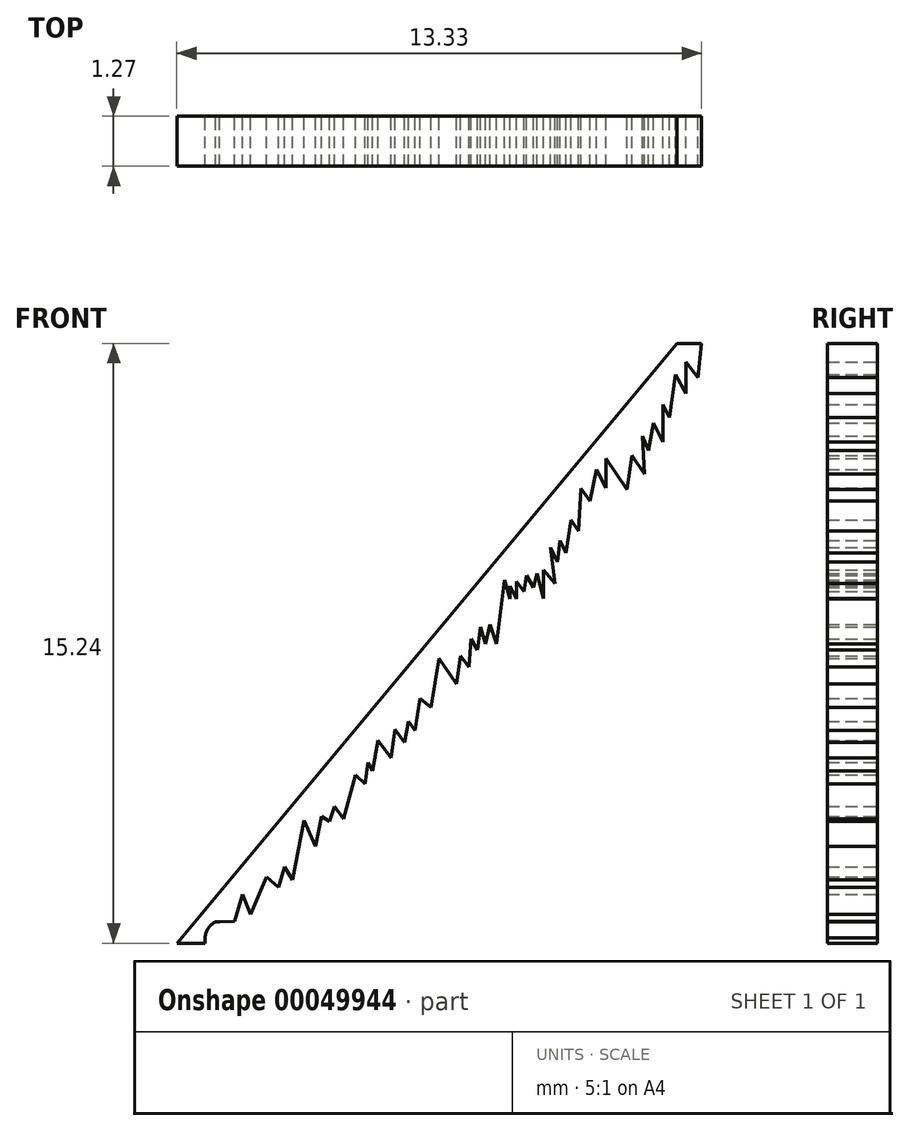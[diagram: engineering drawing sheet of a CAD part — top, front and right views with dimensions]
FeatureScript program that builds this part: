
annotation { "Feature Type Name" : "Feature", "Feature Type Description" : "" }
export const myFeature = defineFeature(function(context is Context, id is Id, definition is map)
    precondition{}
    {
        {
            var Q0;
            Q0=qCreatedBy(makeId("Front.planeOp"),FACE);
            var sketch = newSketch(context, id + "F0", { "sketchPlane" : qUnion([Q0])});
            skLineSegment(sketch, "E0", {"start": v(6.44, 7.64) * mm, "end": v(-6.26, -7.6) * mm});
            skLineSegment(sketch, "E1", {"start": v(-6.26, -7.6) * mm, "end": v(-5.63, -7.6) * mm});
            skLineSegment(sketch, "E2", {"start": v(6.44, 7.64) * mm, "end": v(7.07, 7.64) * mm});
            skLineSegment(sketch, "E3", {"start": v(-4.6, -6.36) * mm, "end": v(-4.17, -6.36) * mm});
            skLineSegment(sketch, "E4", {"start": v(-4.38, -6.36) * mm, "end": v(-4.38, -6.87) * mm});
            skLineSegment(sketch, "E5", {"start": v(-4.38, -6.87) * mm, "end": v(-4.17, -6.36) * mm});
            skLineSegment(sketch, "E6", {"start": v(-4.6, -6.36) * mm, "end": v(-4.38, -6.87) * mm});
            skLineSegment(sketch, "E7", {"start": v(-4.38, -6.87) * mm, "end": v(-3.73, -5.33) * mm});
            skLineSegment(sketch, "E8", {"start": v(-3.73, -5.33) * mm, "end": v(-3.32, -6) * mm});
            skLineSegment(sketch, "E9", {"start": v(-3.32, -6) * mm, "end": v(-3.02, -4.48) * mm});
            skLineSegment(sketch, "E10", {"start": v(-3.02, -4.48) * mm, "end": v(-2.74, -5.14) * mm});
            skLineSegment(sketch, "E11", {"start": v(-2.74, -5.14) * mm, "end": v(-2.48, -3.82) * mm});
            skLineSegment(sketch, "E12", {"start": v(-2.48, -3.82) * mm, "end": v(-2.02, -4.44) * mm});
            skLineSegment(sketch, "E13", {"start": v(-2.02, -4.44) * mm, "end": v(-1.55, -2.7) * mm});
            skLineSegment(sketch, "E14", {"start": v(-1.55, -2.7) * mm, "end": v(-1.3, -3.23) * mm});
            skLineSegment(sketch, "E15", {"start": v(-1.3, -3.23) * mm, "end": v(-1.1, -2.17) * mm});
            skLineSegment(sketch, "E16", {"start": v(-1.48, -3.56) * mm, "end": v(-1.72, -3.33) * mm});
            skLineSegment(sketch, "E17", {"start": v(-2.38, -4.5) * mm, "end": v(-2.59, -4.38) * mm});
            skLineSegment(sketch, "E18", {"start": v(-2.38, -4.5) * mm, "end": v(-2.25, -4.13) * mm});
            skLineSegment(sketch, "E19", {"start": v(-1.48, -3.56) * mm, "end": v(-1.4, -3) * mm});
            skLineSegment(sketch, "E20", {"start": v(-3.53, -5.66) * mm, "end": v(-3.67, -6.18) * mm});
            skLineSegment(sketch, "E21", {"start": v(-3.67, -6.18) * mm, "end": v(-3.98, -5.92) * mm});
            skLineSegment(sketch, "E22", {"start": v(-1.15, -2.45) * mm, "end": v(-0.82, -2.89) * mm});
            skLineSegment(sketch, "E23", {"start": v(-0.82, -2.89) * mm, "end": v(-0.64, -1.61) * mm});
            skLineSegment(sketch, "E24", {"start": v(-0.64, -1.61) * mm, "end": v(-0.21, -2.2) * mm});
            skLineSegment(sketch, "E25", {"start": v(-0.21, -2.2) * mm, "end": v(0, -0.85) * mm});
            skLineSegment(sketch, "E26", {"start": v(-0.72, -2.17) * mm, "end": v(-0.48, -2.5) * mm});
            skLineSegment(sketch, "E27", {"start": v(-0.48, -2.5) * mm, "end": v(-0.38, -1.97) * mm});
            skLineSegment(sketch, "E28", {"start": v(-0.08, -1.38) * mm, "end": v(0.2, -1.61) * mm});
            skLineSegment(sketch, "E29", {"start": v(0.2, -1.61) * mm, "end": v(0.4, -0.36) * mm});
            skLineSegment(sketch, "E30", {"start": v(0.4, -0.36) * mm, "end": v(0.85, -1.01) * mm});
            skLineSegment(sketch, "E31", {"start": v(0.85, -1.01) * mm, "end": v(1.04, 0.4) * mm});
            skLineSegment(sketch, "E32", {"start": v(1.04, 0.4) * mm, "end": v(1.38, -0.14) * mm});
            skLineSegment(sketch, "E33", {"start": v(1.38, -0.14) * mm, "end": v(1.55, 1) * mm});
            skLineSegment(sketch, "E34", {"start": v(1.55, 1) * mm, "end": v(1.86, 0) * mm});
            skLineSegment(sketch, "E35", {"start": v(1.86, 0) * mm, "end": v(2.06, 1.63) * mm});
            skLineSegment(sketch, "E36", {"start": v(2.06, 1.63) * mm, "end": v(2.2, 1.14) * mm});
            skLineSegment(sketch, "E37", {"start": v(2.2, 1.14) * mm, "end": v(2.2, 1.8) * mm});
            skLineSegment(sketch, "E38", {"start": v(2.2, 1.8) * mm, "end": v(2.56, 1.33) * mm});
            skLineSegment(sketch, "E39", {"start": v(2.56, 1.33) * mm, "end": v(2.73, 2.43) * mm});
            skLineSegment(sketch, "E40", {"start": v(2.73, 2.43) * mm, "end": v(3.06, 1.16) * mm});
            skLineSegment(sketch, "E41", {"start": v(3.06, 1.16) * mm, "end": v(3.06, 2.82) * mm});
            skLineSegment(sketch, "E42", {"start": v(3.06, 2.82) * mm, "end": v(3.41, 2.08) * mm});
            skLineSegment(sketch, "E43", {"start": v(3.41, 2.08) * mm, "end": v(3.56, 3.42) * mm});
            skLineSegment(sketch, "E44", {"start": v(3.56, 3.42) * mm, "end": v(3.94, 2.87) * mm});
            skLineSegment(sketch, "E45", {"start": v(3.94, 2.87) * mm, "end": v(4, 3.96) * mm});
            skLineSegment(sketch, "E46", {"start": v(4, 3.96) * mm, "end": v(4.24, 3.63) * mm});
            skLineSegment(sketch, "E47", {"start": v(4.24, 3.63) * mm, "end": v(4.4, 4.44) * mm});
            skLineSegment(sketch, "E48", {"start": v(4.4, 4.44) * mm, "end": v(4.64, 3.96) * mm});
            skLineSegment(sketch, "E49", {"start": v(4.64, 3.96) * mm, "end": v(4.64, 4.72) * mm});
            skLineSegment(sketch, "E50", {"start": v(4.64, 4.72) * mm, "end": v(5.18, 3.92) * mm});
            skLineSegment(sketch, "E51", {"start": v(5.18, 3.92) * mm, "end": v(5.42, 5.66) * mm});
            skLineSegment(sketch, "E52", {"start": v(5.42, 5.66) * mm, "end": v(5.72, 4.92) * mm});
            skLineSegment(sketch, "E53", {"start": v(5.72, 4.92) * mm, "end": v(5.97, 6.31) * mm});
            skLineSegment(sketch, "E54", {"start": v(5.97, 6.31) * mm, "end": v(6.25, 5.76) * mm});
            skLineSegment(sketch, "E55", {"start": v(6.25, 5.76) * mm, "end": v(6.41, 6.85) * mm});
            skLineSegment(sketch, "E56", {"start": v(6.41, 6.85) * mm, "end": v(6.68, 6.36) * mm});
            skLineSegment(sketch, "E57", {"start": v(6.68, 6.36) * mm, "end": v(6.68, 7.17) * mm});
            skLineSegment(sketch, "E58", {"start": v(6.68, 7.17) * mm, "end": v(6.98, 6.77) * mm});
            skLineSegment(sketch, "E59", {"start": v(6.98, 6.77) * mm, "end": v(7.07, 7.64) * mm});
            skLineSegment(sketch, "E60", {"start": v(0.3, -1.01) * mm, "end": v(0.5, -1.24) * mm});
            skPoint(sketch, "E60.startSnap0", {"position": v(0.3, -0.99) * mm});
            skLineSegment(sketch, "E61", {"start": v(0.5, -1.24) * mm, "end": v(0.63, -0.69) * mm});
            skLineSegment(sketch, "E62", {"start": v(0.95, -0.3) * mm, "end": v(1.17, -0.58) * mm});
            skLineSegment(sketch, "E63", {"start": v(1.17, -0.58) * mm, "end": v(1.21, 0.13) * mm});
            skLineSegment(sketch, "E64", {"start": v(1.46, 0.43) * mm, "end": v(1.58, 0) * mm});
            skLineSegment(sketch, "E65", {"start": v(1.58, 0) * mm, "end": v(1.7, 0.5) * mm});
            skLineSegment(sketch, "E66", {"start": v(2.2, 1.47) * mm, "end": v(2.37, 1.14) * mm});
            skLineSegment(sketch, "E67", {"start": v(2.37, 1.14) * mm, "end": v(2.37, 1.58) * mm});
            skLineSegment(sketch, "E68", {"start": v(2.62, 1.74) * mm, "end": v(2.8, 1.44) * mm});
            skLineSegment(sketch, "E69", {"start": v(2.8, 1.44) * mm, "end": v(2.9, 1.8) * mm});
            skLineSegment(sketch, "E70", {"start": v(3.06, 1.88) * mm, "end": v(3.35, 1.54) * mm});
            skLineSegment(sketch, "E71", {"start": v(3.35, 1.54) * mm, "end": v(3.24, 2.45) * mm});
            skLineSegment(sketch, "E72", {"start": v(3.47, 2.63) * mm, "end": v(3.63, 2.31) * mm});
            skLineSegment(sketch, "E73", {"start": v(3.63, 2.31) * mm, "end": v(3.75, 3.15) * mm});
            skLineSegment(sketch, "E74", {"start": v(5.3, 4.8) * mm, "end": v(5.62, 4.32) * mm});
            skPoint(sketch, "E74.endSnap0", {"position": v(4.9, 4.32) * mm});
            skLineSegment(sketch, "E75", {"start": v(5.62, 4.32) * mm, "end": v(5.57, 5.3) * mm});
            skLineSegment(sketch, "E76", {"start": v(5.84, 5.62) * mm, "end": v(6.09, 5.14) * mm});
            skLineSegment(sketch, "E77", {"start": v(6.09, 5.14) * mm, "end": v(6.09, 6.08) * mm});
            skLineSegment(sketch, "E78", {"start": v(-5.17, -7.06) * mm, "end": v(-5.63, -7.06) * mm});
            skLineSegment(sketch, "E79", {"start": v(-5.63, -7.6) * mm, "end": v(-5.63, -7.06) * mm});
            skLineSegment(sketch, "E80", {"start": v(-5.17, -7.06) * mm, "end": v(7.07, 7.64) * mm});
            skLineSegment(sketch, "E81", {"start": v(-5.63, -7.6) * mm, "end": v(-5.57, -7.6) * mm});
            skLineSegment(sketch, "E82", {"start": v(-5.57, -7.6) * mm, "end": v(-5.57, -7.06) * mm});
            skLineSegment(sketch, "E83", {"start": v(-4.6, -6.36) * mm, "end": v(-4.79, -7.04) * mm});
            skLineSegment(sketch, "E84", {"start": v(-5.17, -7.06) * mm, "end": v(-4.79, -7.04) * mm});
            skLineSegment(sketch, "E85", {"start": v(-5.57, -7.6) * mm, "end": v(-5.54, -7.6) * mm});
            skLineSegment(sketch, "E86", {"start": v(-5.54, -7.6) * mm, "end": v(-5.54, -7.06) * mm});
            skArc(sketch, "E87", {"start": v(-5.27, -7.06) * mm, "mid": v(-5.47, -7.23) * mm, "end": v(-5.54, -7.49) * mm});
            skSolve(sketch);
        }
        {
            var Q0;
            Q0 = qSketchRegion(id + "F0", true);
            extrude(context, id + "F1", {"entities" : qUnion([Q0]), "depth" : 1.27 * mm});
        }
    });
